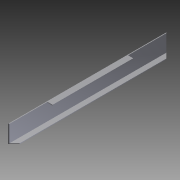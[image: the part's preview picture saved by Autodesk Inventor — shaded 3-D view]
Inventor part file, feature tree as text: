
AUTODESK INVENTOR PART (.ipt)
format: ipt  version: 2012 (Build 160160000, 160)  size: 99,840 bytes
history: native  units: in
note: dims shown in document units (in); Inventor stores cm internally (conversion verified against a paired STEP export)
features: extrude x3, sketch x2
ambient origin geometry x8: Origin, YZ Plane, XZ Plane, XY Plane, X Axis, Y Axis, Z Axis, Center Point
bodies: Solid1 (feature_tree)
feature tree (5):
  extrude  "Extrusion1"  Depth=1.0in
  sketch  "Sketch2"  dims[d2=0.125in d3=0.125in d4=0.125in d5=27.0in d6=0.0in d7=45.0deg d8=0.125in d9=6.5in d10=6.5in d11=28.0in d12=0.0in d13=28.0in d14=0.0in]
  extrude  "Extrusion2"  Depth=0.125in
  extrude  "Extrusion3"  Depth=0.125in
  sketch  "Sketch1"  dims[d0=3.0in d1=1.0in]
